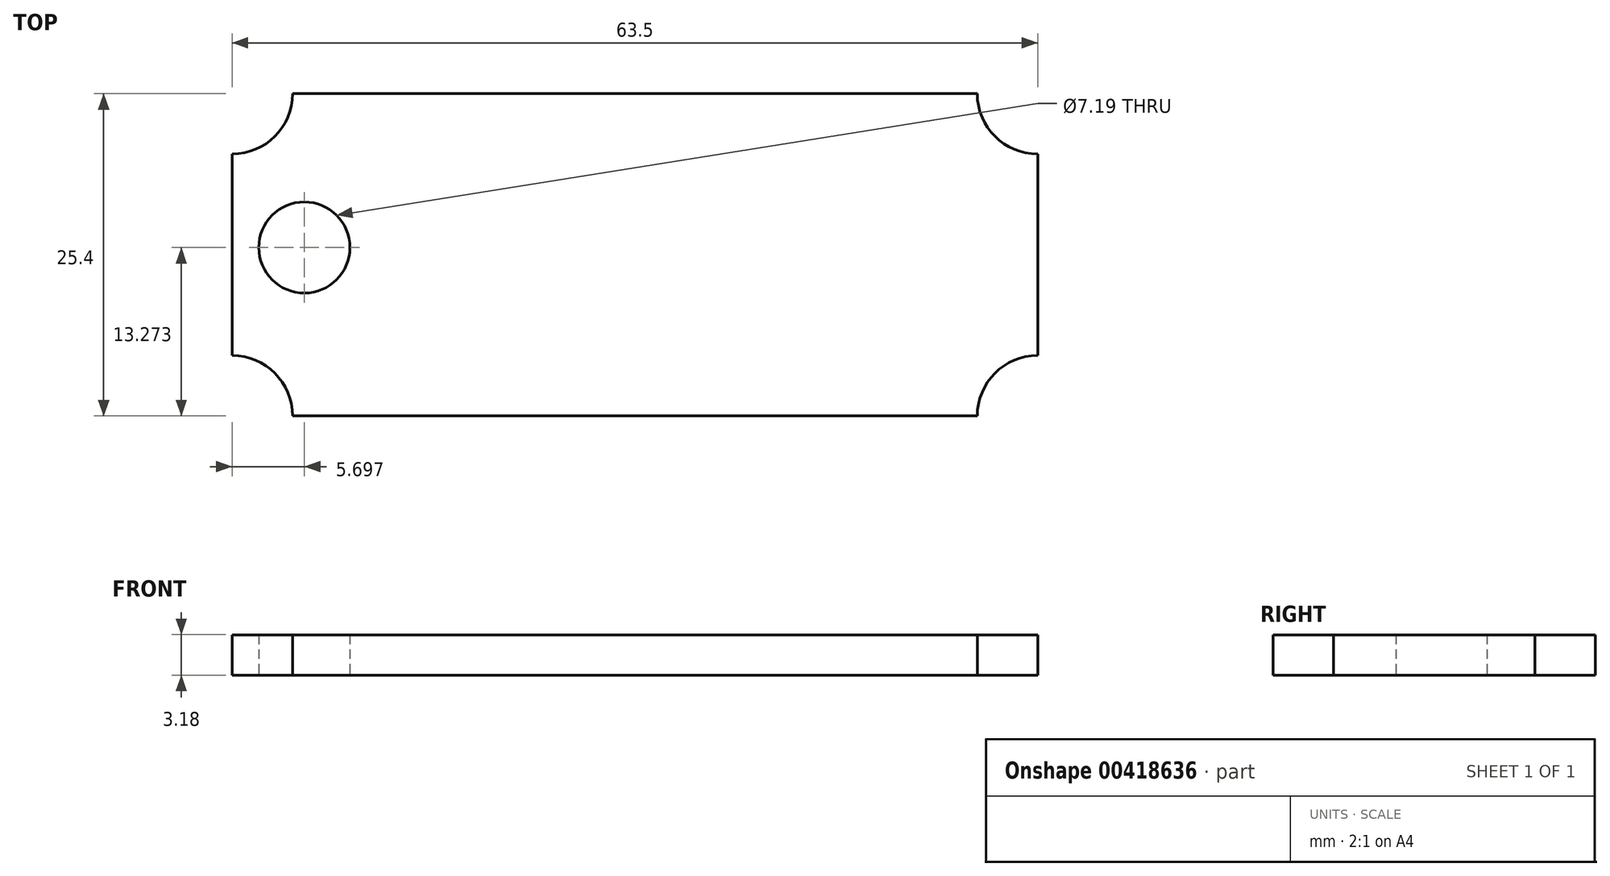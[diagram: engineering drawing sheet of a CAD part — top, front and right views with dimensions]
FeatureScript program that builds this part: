
annotation { "Feature Type Name" : "Feature", "Feature Type Description" : "" }
export const myFeature = defineFeature(function(context is Context, id is Id, definition is map)
    precondition{}
    {
        {
            var Q0;
            Q0=qCreatedBy(makeId("Top.planeOp"),FACE);
            var sketch = newSketch(context, id + "F0", { "sketchPlane" : qUnion([Q0])});
            skLineSegment(sketch, "E0.bottom", {"start": v(4.76, 0) * mm, "end": v(58.74, 0) * mm});
            skLineSegment(sketch, "E0.top", {"start": v(4.76, 25.4) * mm, "end": v(58.74, 25.4) * mm});
            skLineSegment(sketch, "E0.left", {"start": v(0, 4.76) * mm, "end": v(0, 20.64) * mm});
            skLineSegment(sketch, "E0.right", {"start": v(63.5, 4.76) * mm, "end": v(63.5, 20.64) * mm});
            skArc(sketch, "E1", {"start": v(0, 20.64) * mm, "mid": v(3.37, 22.03) * mm, "end": v(4.76, 25.4) * mm});
            skArc(sketch, "E2", {"start": v(4.76, 0) * mm, "mid": v(3.37, 3.37) * mm, "end": v(0, 4.76) * mm});
            skArc(sketch, "E3", {"start": v(58.74, 25.4) * mm, "mid": v(60.13, 22.03) * mm, "end": v(63.5, 20.64) * mm});
            skArc(sketch, "E4", {"start": v(63.5, 4.76) * mm, "mid": v(60.13, 3.37) * mm, "end": v(58.74, 0) * mm});
            skCircle(sketch, "E5", {"center": v(5.7, 13.27) * mm, "radius": 3.6 * mm});
            skSolve(sketch);
        }
        {
            var Q0;
            Q0 = qSketchRegion(id + "F0", true);
            var Q1;
            Q1=makeQuery(id+"F0.imprint","IMPRINT",FACE,{"disambiguationData":[TD([[makeQuery(id+"F0.imprint","IMPRINT",EDGE,{"derivedFrom":sQuery(id+"F0.wireOp",EDGE,"E0.bottom")}),1.0]])]});
            extrude(context, id + "F1", {"entities" : qUnion([Q0, Q1]), "depth" : 3.17 * mm});
        }
    });
